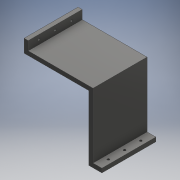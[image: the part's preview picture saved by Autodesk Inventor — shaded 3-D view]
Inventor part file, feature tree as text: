
AUTODESK INVENTOR PART (.ipt)
format: ipt  version: 2016 (Build 200138000, 138)  size: 125,440 bytes
history: native  units: mm
features: hole x6, other x2, thicken_offset x1, sketch x1, extrude x1
ambient origin geometry x8: Origin, YZ Plane, XZ Plane, XY Plane, X Axis, Y Axis, Z Axis, Center Point
bodies: Solid1 (feature_tree)
feature tree (11):
  other  "ConcreteFormwork2"
  thicken_offset  "Thicken1"
  hole  "Hole1"  [1 undecoded]
  hole  "Hole2"  [1 undecoded]
  hole  "Hole3"  [1 undecoded]
  hole  "Hole4"  [1 undecoded]
  hole  "Hole5"  [1 undecoded]
  hole  "Hole6"  [1 undecoded]
  sketch  "Sketch1"  dims[d0=60.0mm d1=300.0mm d2=300.0mm d3=90.0deg d4=60.0mm d5=90.0deg d6=250.0mm d7=0.0mm d8=19.0mm d9=22.0mm d10=20.0mm d11=50.0mm d12=10.0mm d13=6.0mm d14=4.0mm d15=2.0mm d16=90.0deg d17=8.0mm d18=20.594885mm d19=125.0mm d20=20.0mm d21=10.0mm d22=6.0mm d23=4.0mm d24=2.0mm d25=90.0deg d26=8.0mm d27=20.594885mm d28=20.0mm d29=50.0mm d30=10.0mm d31=6.0mm d32=4.0mm d33=2.0mm d34=90.0deg d35=8.0mm d36=20.594885mm d37=50.0mm d38=20.0mm d39=10.0mm d40=6.0mm d41=4.0mm d42=2.0mm d43=90.0deg d44=8.0mm d45=20.594885mm d46=125.0mm d47=20.0mm d48=10.0mm d49=6.0mm d50=4.0mm d51=2.0mm d52=90.0deg d53=8.0mm d54=20.594885mm d55=50.0mm d56=20.0mm d57=10.0mm d58=6.0mm d59=4.0mm d60=2.0mm d61=90.0deg d62=8.0mm d63=20.594885mm]
  other  "Srf1"
  extrude  "ExtrusionSrf1"  Depth=19.0mm
note: 6 required parameter values undecoded (feature->parameter linkage not recoverable at this tier; creation-order binding heuristic only, values carry confidence <= 0.55)
